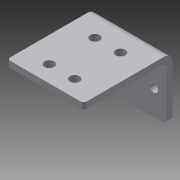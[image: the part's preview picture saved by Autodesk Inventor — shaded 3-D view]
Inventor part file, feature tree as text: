
AUTODESK INVENTOR PART (.ipt)
format: ipt  version: 2014 (Build 180170000, 170)  size: 136,192 bytes
history: native  units: in
note: dims shown in document units (in); Inventor stores cm internally (conversion verified against a paired STEP export)
features: sheet_metal_op x4, sketch x3, other x2, fillet x1, extrude x1
ambient origin geometry x8: Origin, YZ Plane, XZ Plane, XY Plane, X Axis, Y Axis, Z Axis, Center Point
bodies: Solid1 (feature_tree)
feature tree (11):
  sheet_metal_op  "Face1"
  sheet_metal_op  "Flange1"
  fillet  "Fillet1"  Radius=1.5in
  extrude  "Extrusion1"  Depth=0.163in
  sketch  "Sketch1"  dims[d1=1.0in d2=0.163in]
  other  "Plate1"
  sketch  "Sketch2"  dims[d3=0.25in]
  other  "Plate2"
  sheet_metal_op  "Bend1"
  sheet_metal_op  "Corner1"
  sketch  "Sketch3"  dims[d4=0.7874in d6=1.0in d7=0.3937in d9=1.0in d11=0.125in d12=0.125in d13=0.0625in d14=0.25in d15=0.125in d16=1.75in d17=90.0deg d18=0.05in d19=0.5in d20=0.125in d21=0.125in d22=0.0625in d23=1.35in d24=0.75in d25=0.125in d26=0.375in d27=0.19in d28=0.125in d29=0.2265in d30=1.0in d31=0.0in]
